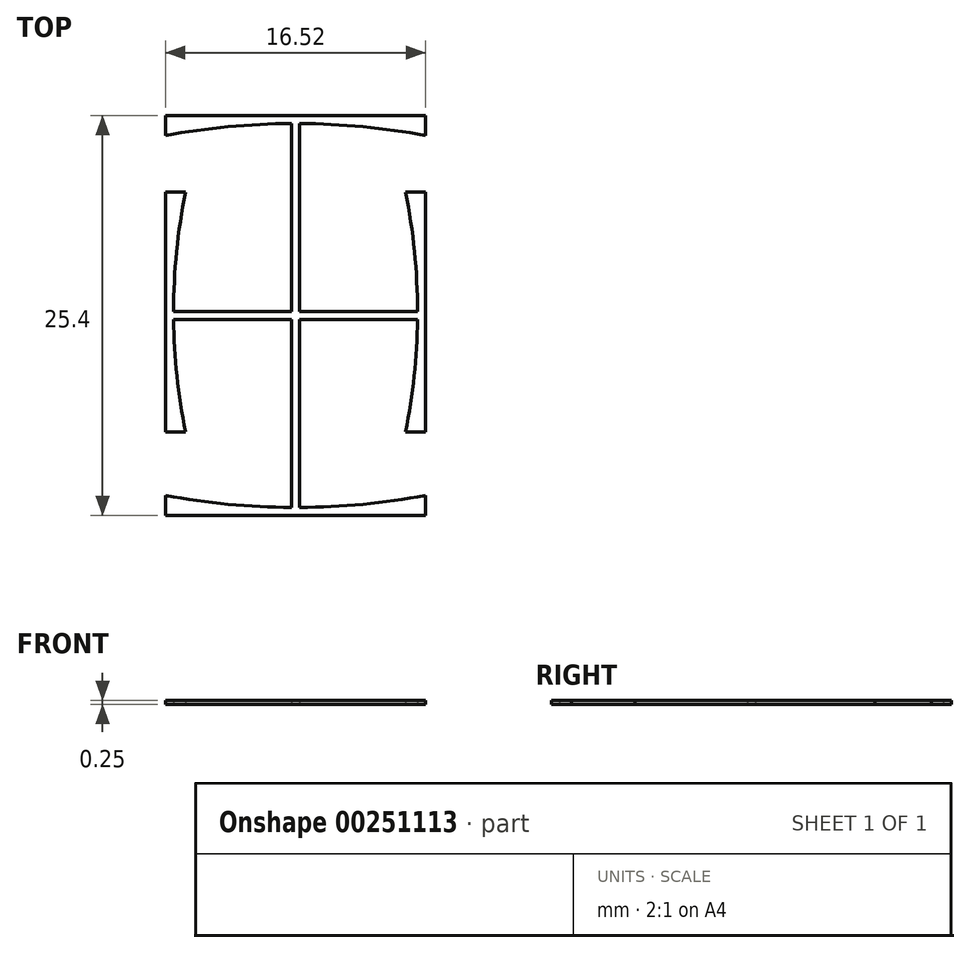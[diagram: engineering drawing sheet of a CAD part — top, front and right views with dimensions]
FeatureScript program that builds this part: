
annotation { "Feature Type Name" : "Feature", "Feature Type Description" : "" }
export const myFeature = defineFeature(function(context is Context, id is Id, definition is map)
    precondition{}
    {
        {
            var Q0;
            Q0=qCreatedBy(makeId("Top.planeOp"),FACE);
            var sketch = newSketch(context, id + "F0", { "sketchPlane" : qUnion([Q0])});
            skLineSegment(sketch, "E0", {"start": v(-8.26, 12.7) * mm, "end": v(8.26, 12.7) * mm});
            skLineSegment(sketch, "E1", {"start": v(-8.26, -12.7) * mm, "end": v(8.26, -12.7) * mm});
            skLineSegment(sketch, "E2", {"start": v(-8.26, 7.84) * mm, "end": v(-8.26, -7.4) * mm});
            skLineSegment(sketch, "E3", {"start": v(8.26, -7.4) * mm, "end": v(8.26, 7.84) * mm});
            skLineSegment(sketch, "E4", {"start": v(-8.26, 12.7) * mm, "end": v(-8.26, 11.43) * mm});
            skLineSegment(sketch, "E5", {"start": v(8.26, 12.7) * mm, "end": v(8.26, 11.43) * mm});
            skLineSegment(sketch, "E6", {"start": v(-8.26, 7.84) * mm, "end": v(-6.99, 7.84) * mm});
            skLineSegment(sketch, "E7", {"start": v(-8.26, -7.4) * mm, "end": v(-6.99, -7.4) * mm});
            skLineSegment(sketch, "E8", {"start": v(8.26, 7.84) * mm, "end": v(6.99, 7.84) * mm});
            skLineSegment(sketch, "E9", {"start": v(8.26, -7.4) * mm, "end": v(6.99, -7.4) * mm});
            skLineSegment(sketch, "E10", {"start": v(8.26, -12.7) * mm, "end": v(8.26, -11.43) * mm});
            skLineSegment(sketch, "E11", {"start": v(-8.26, -12.7) * mm, "end": v(-8.26, -11.43) * mm});
            skArc(sketch, "E12", {"start": v(-6.99, 7.84) * mm, "mid": v(-7.55, 4.06) * mm, "end": v(-7.75, 0.25) * mm});
            skArc(sketch, "E13", {"start": v(6.99, -7.4) * mm, "mid": v(7.53, -3.85) * mm, "end": v(7.74, -0.25) * mm});
            skArc(sketch, "E14", {"start": v(-8.25, -11.43) * mm, "mid": v(-4.27, -11.99) * mm, "end": v(-0.25, -12.2) * mm});
            skArc(sketch, "E15", {"start": v(8.26, 11.43) * mm, "mid": v(4.27, 11.99) * mm, "end": v(0.25, 12.2) * mm});
            skLineSegment(sketch, "E16", {"start": v(-0.25, -12.2) * mm, "end": v(-0.25, -0.25) * mm});
            skLineSegment(sketch, "E17", {"start": v(0.25, 12.2) * mm, "end": v(0.25, 0.25) * mm});
            skLineSegment(sketch, "E18", {"start": v(-7.75, 0.25) * mm, "end": v(-0.25, 0.25) * mm});
            skLineSegment(sketch, "E19", {"start": v(7.74, -0.25) * mm, "end": v(0.25, -0.25) * mm});
            skArc(sketch, "E20.trimOffspring", {"start": v(-7.74, -0.25) * mm, "mid": v(-7.53, -3.85) * mm, "end": v(-6.98, -7.4) * mm});
            skLineSegment(sketch, "E21.trimOffspring", {"start": v(-0.25, 0.25) * mm, "end": v(-0.25, 12.2) * mm});
            skLineSegment(sketch, "E22.trimOffspring", {"start": v(0.25, 0.25) * mm, "end": v(7.75, 0.25) * mm});
            skLineSegment(sketch, "E23.trimOffspring", {"start": v(0.25, -0.25) * mm, "end": v(0.25, -12.2) * mm});
            skLineSegment(sketch, "E24.trimOffspring", {"start": v(-0.25, -0.25) * mm, "end": v(-7.74, -0.25) * mm});
            skArc(sketch, "E25.trimOffspring", {"start": v(7.75, 0.25) * mm, "mid": v(7.55, 4.06) * mm, "end": v(6.99, 7.84) * mm});
            skArc(sketch, "E26.trimOffspring", {"start": v(-0.25, 12.2) * mm, "mid": v(-4.27, 11.99) * mm, "end": v(-8.26, 11.43) * mm});
            skArc(sketch, "E27.trimOffspring", {"start": v(0.25, -12.2) * mm, "mid": v(4.27, -11.99) * mm, "end": v(8.26, -11.43) * mm});
            skSolve(sketch);
        }
        {
            var Q0;
            Q0 = qSketchRegion(id + "F0", true);
            extrude(context, id + "F1", {"entities" : qUnion([Q0]), "depth" : 0.25 * mm});
        }
    });
